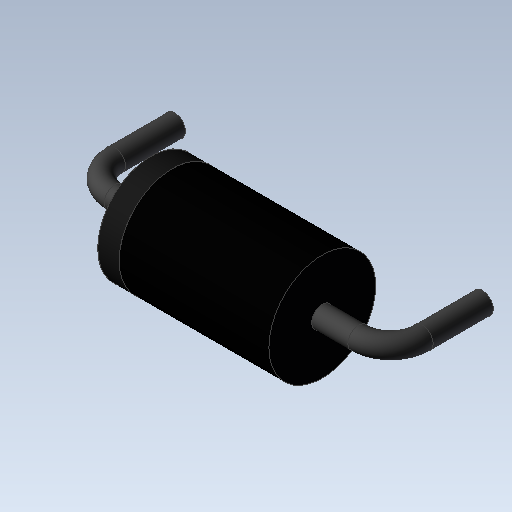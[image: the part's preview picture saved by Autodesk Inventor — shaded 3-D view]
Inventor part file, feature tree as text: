
AUTODESK INVENTOR PART (.ipt)
format: ipt  version: 2020 (Build 240168000, 168)  size: 118,784 bytes
history: imported  units: in
note: dims shown in document units (in); Inventor stores cm internally (conversion verified against a paired STEP export)
features: imported_body x1
ambient origin geometry x8: Origin, YZ Plane, XZ Plane, XY Plane, X Axis, Y Axis, Z Axis, Center Point
bodies: Solid1 (imported_parasolid), Body2 (imported_parasolid)
feature tree (1):
  imported_body  NMx_Import_Brep_tag  [imported B-rep: ~15 faces, bbox_mm=[15.28, 0.53, 4.57]]
